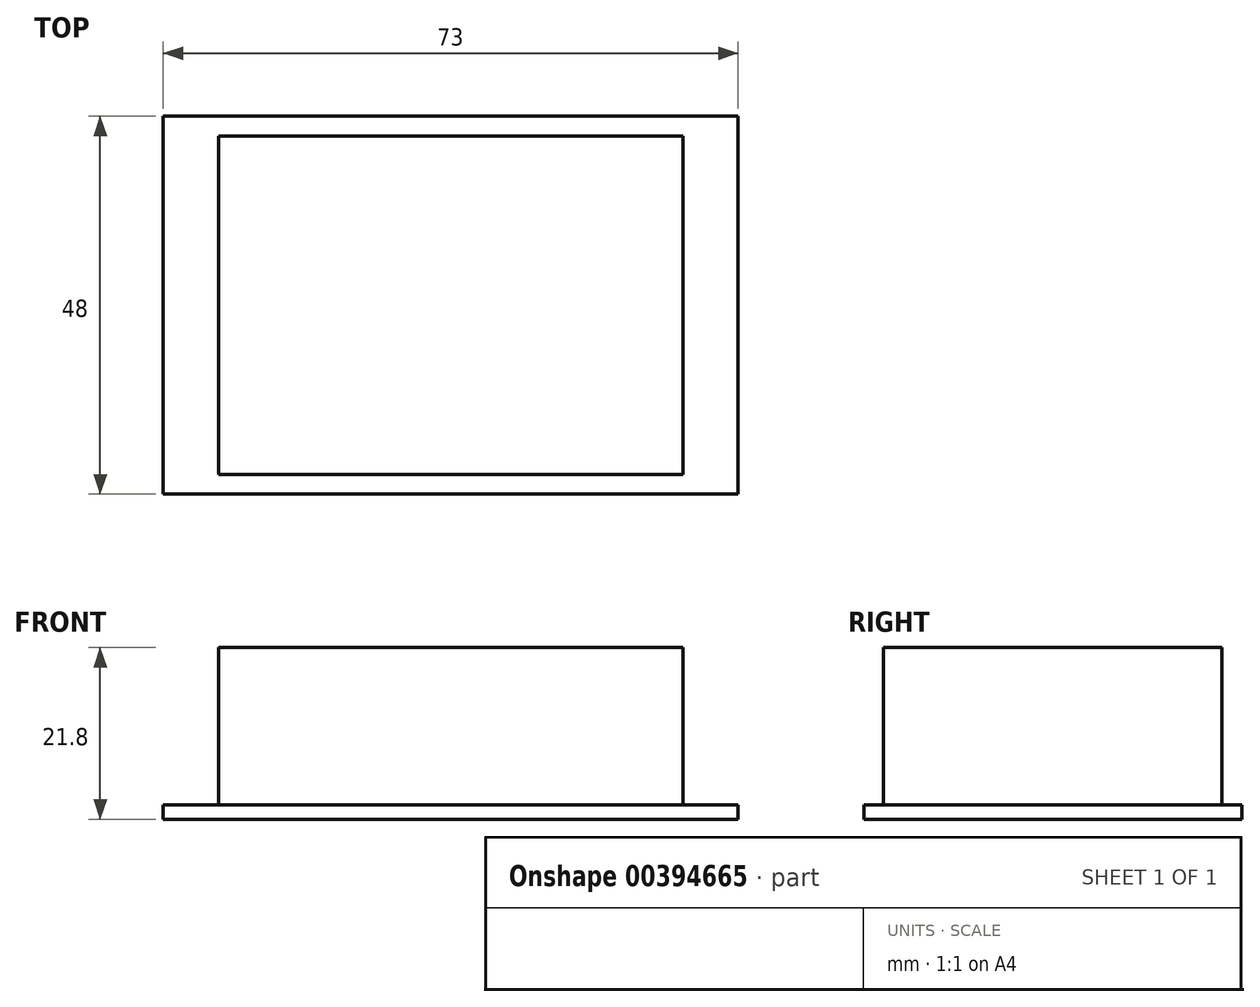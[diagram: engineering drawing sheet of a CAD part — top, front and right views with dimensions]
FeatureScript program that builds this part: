
annotation { "Feature Type Name" : "Feature", "Feature Type Description" : "" }
export const myFeature = defineFeature(function(context is Context, id is Id, definition is map)
    precondition{}
    {
        {
            var Q0;
            Q0=qCreatedBy(makeId("Top.planeOp"),FACE);
            var sketch = newSketch(context, id + "F0", { "sketchPlane" : qUnion([Q0])});
            skLineSegment(sketch, "E0.bottom", {"start": v(-36.5, 24) * mm, "end": v(36.5, 24) * mm});
            skLineSegment(sketch, "E0.top", {"start": v(-36.5, -24) * mm, "end": v(36.5, -24) * mm});
            skLineSegment(sketch, "E0.left", {"start": v(-36.5, 24) * mm, "end": v(-36.5, -24) * mm});
            skLineSegment(sketch, "E0.right", {"start": v(36.5, 24) * mm, "end": v(36.5, -24) * mm});
            skLineSegment(sketch, "E1", {"start": v(-36.5, 24) * mm, "end": v(36.5, -24) * mm, "construction": true});
            skSolve(sketch);
        }
        {
            var Q0;
            Q0=makeQuery(id+"F0.imprint","IMPRINT",FACE,{"disambiguationData":[TD([[makeQuery(id+"F0.imprint","IMPRINT",EDGE,{"derivedFrom":sQuery(id+"F0.wireOp",EDGE,"E0.bottom")}),-1.0]])]});
            extrude(context, id + "F1", {"entities" : qUnion([Q0]), "depth" : 1.8 * mm});
        }
        {
            var Q0;
            Q0=makeQuery(id+"F1.opExtrude","CAP_FACE",FACE,{"disambiguationData":[OSD([sQuery(id+"F0.wireOp",EDGE,"E0.bottom"),sQuery(id+"F0.wireOp",EDGE,"E0.top"),sQuery(id+"F0.wireOp",EDGE,"E0.left"),sQuery(id+"F0.wireOp",EDGE,"E0.right")])],"isStart":false});
            var sketch = newSketch(context, id + "F2", { "sketchPlane" : qUnion([Q0])});
            skLineSegment(sketch, "E2.bottom", {"start": v(-29.5, -21.5) * mm, "end": v(29.5, -21.5) * mm});
            skLineSegment(sketch, "E2.top", {"start": v(-29.5, 21.5) * mm, "end": v(29.5, 21.5) * mm});
            skLineSegment(sketch, "E2.left", {"start": v(-29.5, -21.5) * mm, "end": v(-29.5, 21.5) * mm});
            skLineSegment(sketch, "E2.right", {"start": v(29.5, -21.5) * mm, "end": v(29.5, 21.5) * mm});
            skLineSegment(sketch, "E3", {"start": v(-29.5, 21.5) * mm, "end": v(29.5, -21.5) * mm, "construction": true});
            skSolve(sketch);
        }
        {
            var Q0;
            Q0 = qSketchRegion(id + "F2", true);
            extrude(context, id + "F3", {"entities" : qUnion([Q0]), "operationType" : NewBodyOperationType.ADD, "depth" : 20 * mm});
        }
    });
